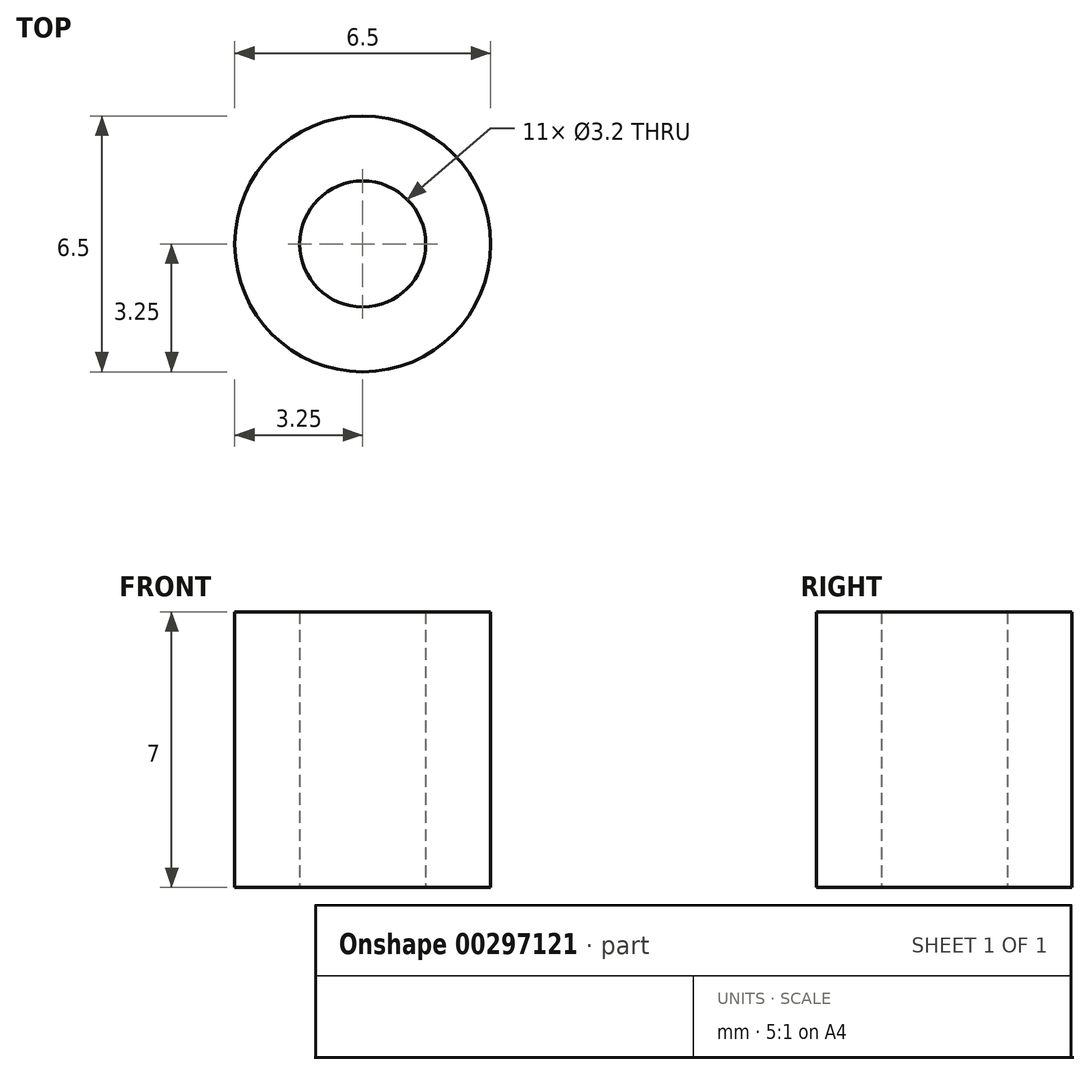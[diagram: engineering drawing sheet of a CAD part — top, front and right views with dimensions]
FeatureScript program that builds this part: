
annotation { "Feature Type Name" : "Feature", "Feature Type Description" : "" }
export const myFeature = defineFeature(function(context is Context, id is Id, definition is map)
    precondition{}
    {
        {
            var Q0;
            Q0=qCreatedBy(makeId("Top.planeOp"),FACE);
            var sketch = newSketch(context, id + "F0", { "sketchPlane" : qUnion([Q0])});
            skCircle(sketch, "E0", {"center": v(0, 0) * mm, "radius": 1.6 * mm});
            skCircle(sketch, "E1", {"center": v(0, 0) * mm, "radius": 3.25 * mm});
            skSolve(sketch);
        }
        {
            var Q0;
            Q0 = qSketchRegion(id + "F0", true);
            extrude(context, id + "F1", {"entities" : qUnion([Q0]), "depth" : 7 * mm});
        }
    });
